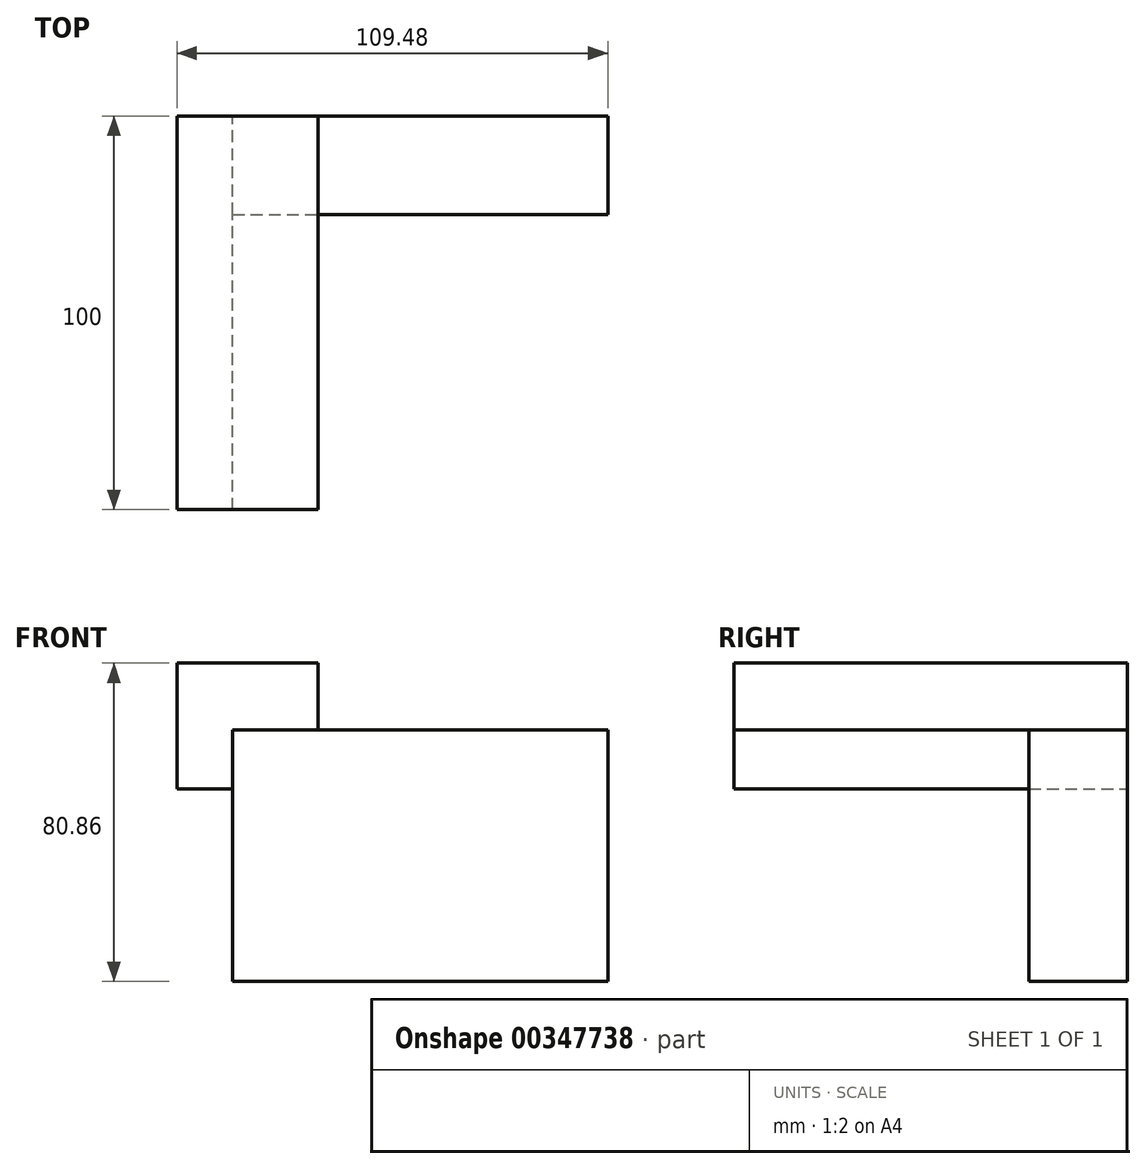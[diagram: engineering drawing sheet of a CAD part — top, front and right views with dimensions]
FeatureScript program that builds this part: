
annotation { "Feature Type Name" : "Feature", "Feature Type Description" : "" }
export const myFeature = defineFeature(function(context is Context, id is Id, definition is map)
    precondition{}
    {
        {
            var Q0;
            Q0=qCreatedBy(makeId("Front.planeOp"),FACE);
            var sketch = newSketch(context, id + "F0", { "sketchPlane" : qUnion([Q0])});
            skLineSegment(sketch, "E0.bottom", {"start": v(-36.96, 27.23) * mm, "end": v(58.35, 27.23) * mm});
            skLineSegment(sketch, "E0.top", {"start": v(-36.96, -36.68) * mm, "end": v(58.35, -36.68) * mm});
            skLineSegment(sketch, "E0.left", {"start": v(-36.96, 27.23) * mm, "end": v(-36.96, -36.68) * mm});
            skLineSegment(sketch, "E0.right", {"start": v(58.35, 27.23) * mm, "end": v(58.35, -36.68) * mm});
            skLineSegment(sketch, "E1.bottom", {"start": v(-51.13, 44.18) * mm, "end": v(-15.28, 44.18) * mm});
            skLineSegment(sketch, "E1.top", {"start": v(-51.13, 12.23) * mm, "end": v(-15.28, 12.23) * mm});
            skLineSegment(sketch, "E1.left", {"start": v(-51.13, 44.18) * mm, "end": v(-51.13, 12.23) * mm});
            skLineSegment(sketch, "E1.right", {"start": v(-15.28, 44.18) * mm, "end": v(-15.28, 12.23) * mm});
            skSolve(sketch);
        }
        {
            var Q0;
            {var subQ2=sQuery(id+"F0.wireOp",EDGE,"E0.top");Q0=makeQuery(id+"F0.imprint","IMPRINT",FACE,{"disambiguationData":[TD([[makeQuery(id+"F0.imprint","IMPRINT",EDGE,{"derivedFrom":subQ2}),1.0]])]});}
            var Q1;
            {var subQ0=sQuery(id+"F0.wireOp",EDGE,"E0.left");var subQ1=sQuery(id+"F0.wireOp",EDGE,"E0.bottom");var subQ2=makeQuery(id+"F0.imprint","INTERSECT",VERTEX,{"derivedFrom":[subQ1,subQ0]});Q1=makeQuery(id+"F0.imprint","IMPRINT",FACE,{"disambiguationData":[TD([[makeQuery(id+"F0.imprint","IMPRINT",EDGE,{"disambiguationData":[TD([[subQ2,-1.0]])],"derivedFrom":subQ1}),-1.0]])]});}
            extrude(context, id + "F1", {"entities" : qUnion([Q0, Q1]), "depth" : 25 * mm});
        }
        {
            var Q0;
            {var subQ4=sQuery(id+"F0.wireOp",EDGE,"E1.bottom");Q0=makeQuery(id+"F0.imprint","IMPRINT",FACE,{"disambiguationData":[TD([[makeQuery(id+"F0.imprint","IMPRINT",EDGE,{"derivedFrom":subQ4}),-1.0]])]});}
            extrude(context, id + "F2", {"entities" : qUnion([Q0]), "operationType" : NewBodyOperationType.ADD, "depth" : 100 * mm});
        }
    });
